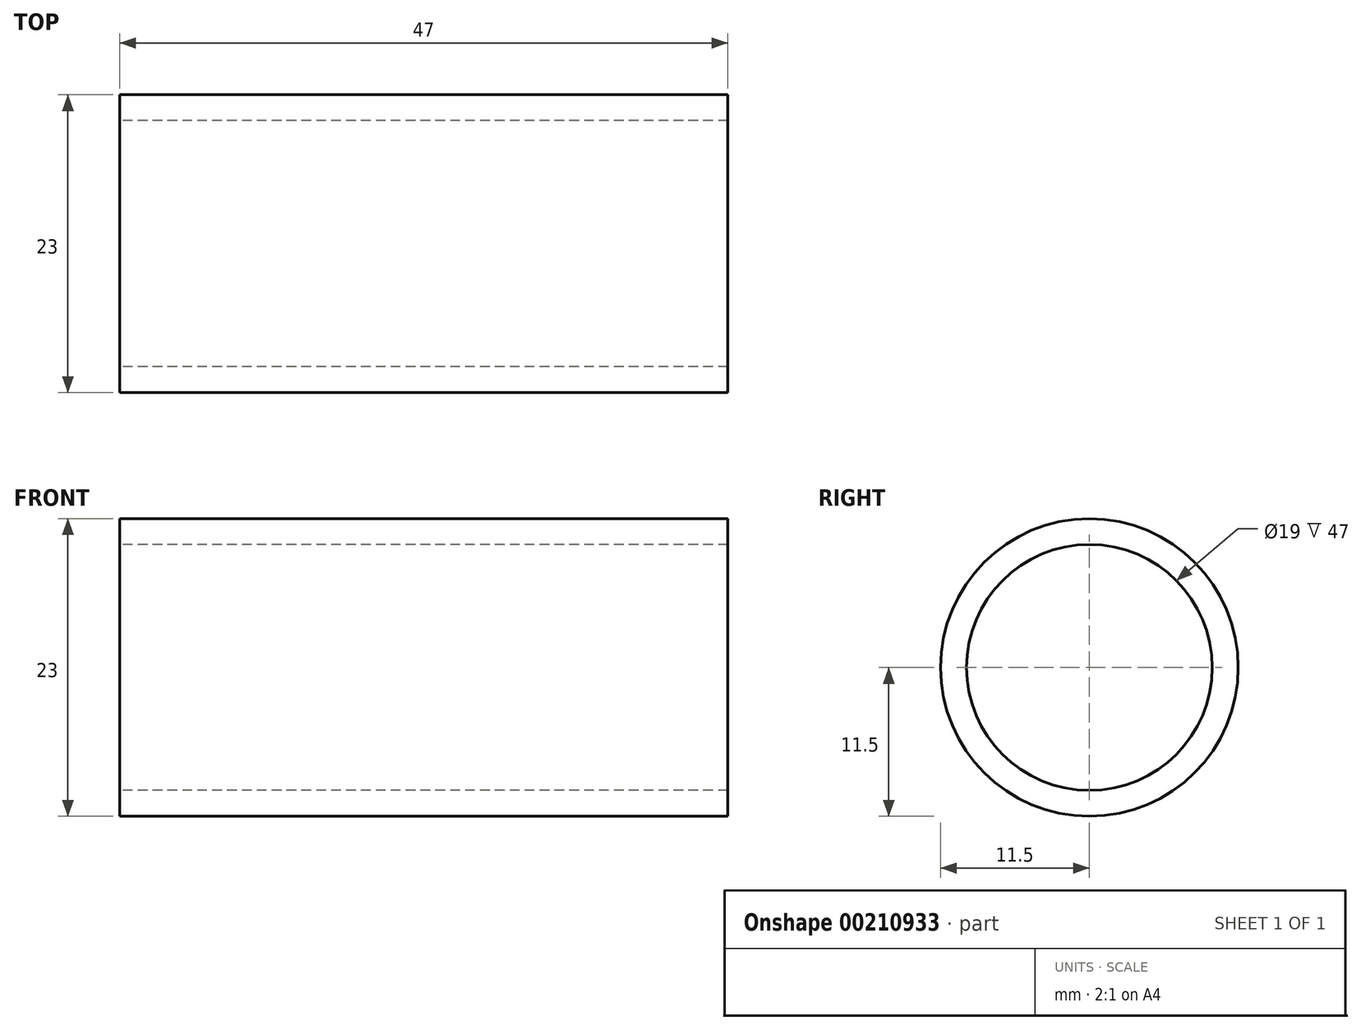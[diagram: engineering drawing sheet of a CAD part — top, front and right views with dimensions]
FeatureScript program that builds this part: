
annotation { "Feature Type Name" : "Feature", "Feature Type Description" : "" }
export const myFeature = defineFeature(function(context is Context, id is Id, definition is map)
    precondition{}
    {
        {
            var Q0;
            Q0=qCreatedBy(makeId("Front.planeOp"),FACE);
            var sketch = newSketch(context, id + "F0", { "sketchPlane" : qUnion([Q0])});
            skLineSegment(sketch, "E0.bottom", {"start": v(-23.5, 9.5) * mm, "end": v(23.5, 9.5) * mm});
            skLineSegment(sketch, "E0.top", {"start": v(-23.5, 11.5) * mm, "end": v(23.5, 11.5) * mm});
            skLineSegment(sketch, "E0.left", {"start": v(-23.5, 9.5) * mm, "end": v(-23.5, 11.5) * mm});
            skLineSegment(sketch, "E0.right", {"start": v(23.5, 9.5) * mm, "end": v(23.5, 11.5) * mm});
            skPoint(sketch, "E0.middle", {"position": v(0, 10.5) * mm});
            skLineSegment(sketch, "E1.bottom", {"start": v(-23.5, 9.5) * mm, "end": v(-21.5, 9.5) * mm});
            skLineSegment(sketch, "E1.top", {"start": v(-23.5, 6) * mm, "end": v(-21.5, 6) * mm});
            skLineSegment(sketch, "E1.left", {"start": v(-23.5, 9.5) * mm, "end": v(-23.5, 6) * mm});
            skLineSegment(sketch, "E1.right", {"start": v(-21.5, 9.5) * mm, "end": v(-21.5, 6) * mm});
            skSolve(sketch);
        }
        {
            var Q0;
            Q0=qCreatedBy(makeId("Front.planeOp"),FACE);
            var sketch = newSketch(context, id + "F1", { "sketchPlane" : qUnion([Q0])});
            skLineSegment(sketch, "E2", {"start": v(-38.96, 0) * mm, "end": v(38.77, 0) * mm});
            skSolve(sketch);
        }
        {
            var Q0;
            Q0=makeQuery(id+"F0.imprint","IMPRINT",FACE,{"disambiguationData":[TD([[makeQuery(id+"F0.imprint","IMPRINT",EDGE,{"derivedFrom":sQuery(id+"F0.wireOp",EDGE,"E0.bottom")}),1.0]])]});
            var Q1;
            Q1=makeQuery(id+"F0.imprint","IMPRINT",FACE,{"disambiguationData":[TD([[makeQuery(id+"F0.imprint","IMPRINT",EDGE,{"derivedFrom":sQuery(id+"F0.wireOp",EDGE,"E1.bottom")}),-1.0]])]});
            var Q2;
            Q2=sQuery(id+"F1.wireOp",EDGE,"E2");
            revolve(context, id + "F2", {"entities" : qUnion([Q0, Q1]), "axis" : qUnion([Q2]), "revolveType" : RevolveType.FULL});
        }
    });
